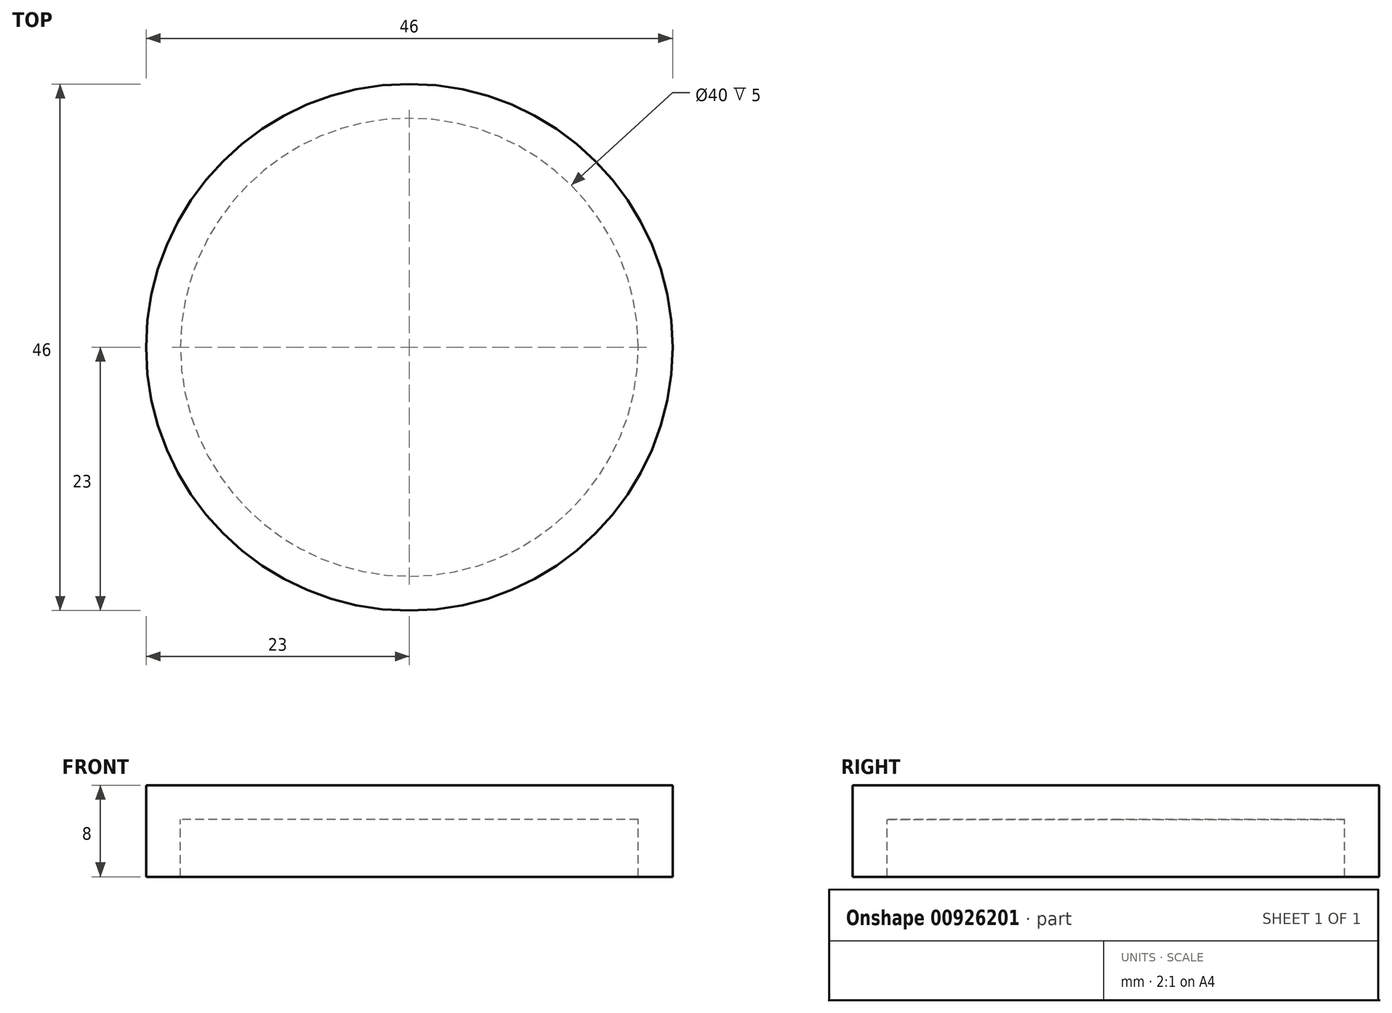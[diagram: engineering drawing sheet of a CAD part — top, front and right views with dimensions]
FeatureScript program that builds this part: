
annotation { "Feature Type Name" : "Feature", "Feature Type Description" : "" }
export const myFeature = defineFeature(function(context is Context, id is Id, definition is map)
    precondition{}
    {
        {
            var Q0;
            Q0=qCreatedBy(makeId("Front.planeOp"),FACE);
            var sketch = newSketch(context, id + "F0", { "sketchPlane" : qUnion([Q0])});
            skLineSegment(sketch, "E0", {"start": v(20, 0) * mm, "end": v(23, 0) * mm});
            skLineSegment(sketch, "E1", {"start": v(23, 0) * mm, "end": v(23, 8) * mm});
            skLineSegment(sketch, "E2", {"start": v(23, 8) * mm, "end": v(0, 8) * mm});
            skLineSegment(sketch, "E3", {"start": v(0, 8) * mm, "end": v(0, 5) * mm});
            skLineSegment(sketch, "E4", {"start": v(0, 5) * mm, "end": v(20, 5) * mm});
            skLineSegment(sketch, "E5", {"start": v(20, 5) * mm, "end": v(20, 0) * mm});
            skSolve(sketch);
        }
        {
            var Q0;
            Q0=makeQuery(id+"F0.imprint","IMPRINT",FACE,{"disambiguationData":[TD([[makeQuery(id+"F0.imprint","IMPRINT",EDGE,{"derivedFrom":sQuery(id+"F0.wireOp",EDGE,"E0")}),1.0]])]});
            var Q1;
            Q1=sQuery(id+"F0.wireOp",EDGE,"E3");
            revolve(context, id + "F1", {"surfaceOperationType" : NewSurfaceOperationType.NEW, "entities" : qUnion([Q0]), "axis" : qUnion([Q1]), "revolveType" : RevolveType.FULL});
        }
    });
